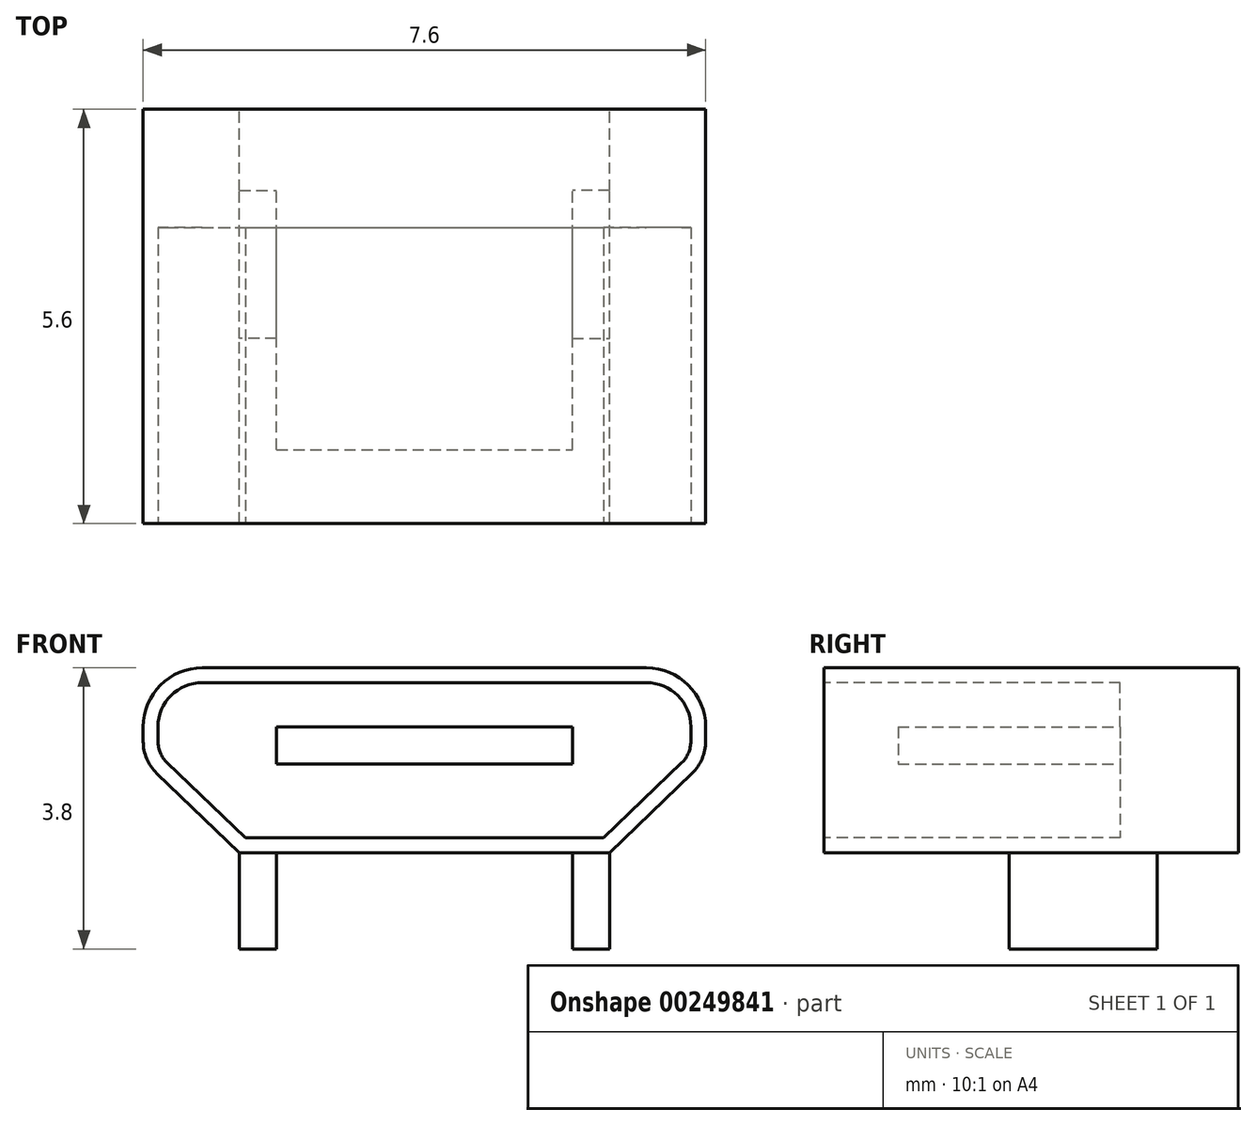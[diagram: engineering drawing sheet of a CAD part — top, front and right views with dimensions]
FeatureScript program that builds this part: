
annotation { "Feature Type Name" : "Feature", "Feature Type Description" : "" }
export const myFeature = defineFeature(function(context is Context, id is Id, definition is map)
    precondition{}
    {
        {
            var Q0;
            Q0=qCreatedBy(makeId("Front.planeOp"),FACE);
            var sketch = newSketch(context, id + "F0", { "sketchPlane" : qUnion([Q0])});
            skLineSegment(sketch, "E0.bottom", {"start": v(0, 0) * mm, "end": v(7.6, 0) * mm, "construction": true});
            skLineSegment(sketch, "E0.top", {"start": v(0, 2.5) * mm, "end": v(7.6, 2.5) * mm, "construction": true});
            skLineSegment(sketch, "E0.left", {"start": v(0, 0) * mm, "end": v(0, 2.5) * mm, "construction": true});
            skLineSegment(sketch, "E0.right", {"start": v(7.6, 0) * mm, "end": v(7.6, 2.5) * mm, "construction": true});
            skLineSegment(sketch, "E1", {"start": v(0, 1.25) * mm, "end": v(1.3, 0) * mm});
            skLineSegment(sketch, "E2", {"start": v(7.6, 1.25) * mm, "end": v(6.3, 0) * mm});
            skLineSegment(sketch, "E3", {"start": v(0, 1.25) * mm, "end": v(0, 2.5) * mm});
            skLineSegment(sketch, "E4", {"start": v(0, 2.5) * mm, "end": v(7.6, 2.5) * mm});
            skLineSegment(sketch, "E5", {"start": v(7.6, 2.5) * mm, "end": v(7.6, 1.25) * mm});
            skLineSegment(sketch, "E6", {"start": v(1.3, 0) * mm, "end": v(6.3, 0) * mm});
            skSolve(sketch);
        }
        {
            var Q0;
            Q0 = qSketchRegion(id + "F0", true);
            extrude(context, id + "F1", {"entities" : qUnion([Q0]), "depth" : 5.6 * mm});
        }
        {
            var Q0;
            Q0=makeQuery(id+"F1.opExtrude","SWEPT_EDGE",EDGE,{"disambiguationData":[OSD([sQuery(id+"F0.wireOp",EDGE,"E3"),sQuery(id+"F0.wireOp",EDGE,"E4")])]});
            var Q1;
            Q1=makeQuery(id+"F1.opExtrude","SWEPT_EDGE",EDGE,{"disambiguationData":[OSD([sQuery(id+"F0.wireOp",EDGE,"E4"),sQuery(id+"F0.wireOp",EDGE,"E5")])]});
            fillet(context, id + "F2", {"entities" : qUnion([Q0, Q1]), "radius" : 0.8 * mm, "tangentPropagation" : true, "allowEdgeOverflow" : false});
        }
        {
            var Q0;
            Q0=makeQuery(id+"F1.opExtrude","SWEPT_EDGE",EDGE,{"disambiguationData":[OSD([sQuery(id+"F0.wireOp",EDGE,"E1"),sQuery(id+"F0.wireOp",EDGE,"E3")])]});
            var Q1;
            Q1=makeQuery(id+"F1.opExtrude","SWEPT_EDGE",EDGE,{"disambiguationData":[OSD([sQuery(id+"F0.wireOp",EDGE,"E2"),sQuery(id+"F0.wireOp",EDGE,"E5")])]});
            fillet(context, id + "F3", {"entities" : qUnion([Q0, Q1]), "radius" : 0.6 * mm, "tangentPropagation" : true, "allowEdgeOverflow" : false});
        }
        {
            var Q0;
            Q0=makeQuery(id+"F1.opExtrude","SWEPT_FACE",FACE,{"disambiguationData":[OSD([sQuery(id+"F0.wireOp",EDGE,"E6")])]});
            var sketch = newSketch(context, id + "F4", { "sketchPlane" : qUnion([Q0])});
            skLineSegment(sketch, "E7.right", {"start": v(1.8, 3.1) * mm, "end": v(1.8, 1.1) * mm});
            skLineSegment(sketch, "E8.top", {"start": v(6.3, 1.1) * mm, "end": v(5.8, 1.1) * mm});
            skLineSegment(sketch, "E8.right", {"start": v(5.8, 3.1) * mm, "end": v(5.8, 1.1) * mm});
            skLineSegment(sketch, "E9", {"start": v(1.8, 3.1) * mm, "end": v(1.3, 3.1) * mm});
            skLineSegment(sketch, "E10", {"start": v(5.8, 3.1) * mm, "end": v(6.3, 3.1) * mm});
            skLineSegment(sketch, "E11", {"start": v(6.3, 3.1) * mm, "end": v(6.3, 1.1) * mm});
            skLineSegment(sketch, "E12", {"start": v(1.3, 3.1) * mm, "end": v(1.3, 1.1) * mm});
            skLineSegment(sketch, "E13", {"start": v(1.3, 1.1) * mm, "end": v(1.8, 1.1) * mm});
            skSolve(sketch);
        }
        {
            var Q0;
            Q0 = qSketchRegion(id + "F4", true);
            extrude(context, id + "F5", {"entities" : qUnion([Q0]), "operationType" : NewBodyOperationType.ADD, "depth" : 1.3 * mm});
        }
        {
            var Q0;
            Q0=makeQuery(id+"F5.boolean.opBoolean","MERGE",FACE,{"derivedFrom":[makeQuery(id+"F1.opExtrude","CAP_FACE",FACE,{"disambiguationData":[OSD([sQuery(id+"F0.wireOp",EDGE,"E1"),sQuery(id+"F0.wireOp",EDGE,"E2"),sQuery(id+"F0.wireOp",EDGE,"E3"),sQuery(id+"F0.wireOp",EDGE,"E4"),sQuery(id+"F0.wireOp",EDGE,"E5"),sQuery(id+"F0.wireOp",EDGE,"E6")])],"isStart":false}),makeQuery(id+"F5.opExtrude","SWEPT_FACE",FACE,{"disambiguationData":[OSD([sQuery(id+"F4.wireOp",EDGE,"E7.bottom")])]}),makeQuery(id+"F5.opExtrude","SWEPT_FACE",FACE,{"disambiguationData":[OSD([sQuery(id+"F4.wireOp",EDGE,"E8.bottom")])]})]});
            var sketch = newSketch(context, id + "F6", { "sketchPlane" : qUnion([Q0])});
            skLineSegment(sketch, "E14", {"start": v(0.8, 2.3) * mm, "end": v(6.8, 2.3) * mm});
            skLineSegment(sketch, "E15", {"start": v(1.38, 0.2) * mm, "end": v(6.22, 0.2) * mm});
            skArc(sketch, "E16", {"start": v(0.8, 2.3) * mm, "mid": v(0.38, 2.12) * mm, "end": v(0.2, 1.7) * mm});
            skArc(sketch, "E17", {"start": v(7.4, 1.7) * mm, "mid": v(7.22, 2.12) * mm, "end": v(6.8, 2.3) * mm});
            skLineSegment(sketch, "E18", {"start": v(0.32, 1.22) * mm, "end": v(1.38, 0.2) * mm});
            skArc(sketch, "E19", {"start": v(0.2, 1.5) * mm, "mid": v(0.23, 1.35) * mm, "end": v(0.32, 1.22) * mm});
            skArc(sketch, "E20", {"start": v(7.28, 1.22) * mm, "mid": v(7.37, 1.35) * mm, "end": v(7.4, 1.5) * mm});
            skLineSegment(sketch, "E21", {"start": v(7.4, 1.7) * mm, "end": v(7.4, 1.5) * mm});
            skLineSegment(sketch, "E22", {"start": v(7.28, 1.22) * mm, "end": v(6.22, 0.2) * mm});
            skLineSegment(sketch, "E23", {"start": v(0.2, 1.7) * mm, "end": v(0.2, 1.5) * mm});
            skSolve(sketch);
        }
        {
            var Q0;
            Q0 = qSketchRegion(id + "F6", true);
            extrude(context, id + "F7", {"entities" : qUnion([Q0]), "operationType" : NewBodyOperationType.REMOVE, "oppositeDirection" : true, "depth" : 4 * mm});
        }
        {
            var Q0;
            Q0=makeQuery(id+"F7.boolean.opBoolean","COPY",FACE,{"derivedFrom":makeQuery(id+"F7.opExtrude","CAP_FACE",FACE,{"disambiguationData":[OSD([sQuery(id+"F6.wireOp",EDGE,"E14"),sQuery(id+"F6.wireOp",EDGE,"E15"),sQuery(id+"F6.wireOp",EDGE,"E16"),sQuery(id+"F6.wireOp",EDGE,"E17"),sQuery(id+"F6.wireOp",EDGE,"E18"),sQuery(id+"F6.wireOp",EDGE,"E19"),sQuery(id+"F6.wireOp",EDGE,"E20"),sQuery(id+"F6.wireOp",EDGE,"E21"),sQuery(id+"F6.wireOp",EDGE,"E22"),sQuery(id+"F6.wireOp",EDGE,"E23")])],"isStart":false})});
            var sketch = newSketch(context, id + "F8", { "sketchPlane" : qUnion([Q0])});
            skLineSegment(sketch, "E24.bottom", {"start": v(1.8, 1.7) * mm, "end": v(5.8, 1.7) * mm});
            skLineSegment(sketch, "E24.top", {"start": v(1.8, 1.2) * mm, "end": v(5.8, 1.2) * mm});
            skLineSegment(sketch, "E24.left", {"start": v(1.8, 1.7) * mm, "end": v(1.8, 1.2) * mm});
            skLineSegment(sketch, "E24.right", {"start": v(5.8, 1.7) * mm, "end": v(5.8, 1.2) * mm});
            skLineSegment(sketch, "E25", {"start": v(3.8, 2.3) * mm, "end": v(3.8, 0.2) * mm, "construction": true});
            skSolve(sketch);
        }
        {
            var Q0;
            Q0 = qSketchRegion(id + "F8", true);
            extrude(context, id + "F9", {"entities" : qUnion([Q0]), "operationType" : NewBodyOperationType.ADD, "depth" : 3 * mm});
        }
    });
